# Revit family: Zumtobel VIVO II S
name_source: partatom
category: Lighting Fixtures
revit_build: Autodesk Revit 2016 (Build: 20150220_1215(x64)
units: mm (PartAtom-declared; Revit-internal decimal feet)

## family parameters
Cut with Voids When Loaded = No
Host = Face
Light Source = No
OmniClass Number = 23.80.70.11
OmniClass Title = Luminaries for Internal Lighting
Part Type = Normal
Room Calculation Point = No
Round Connector Dimension = Use Diameter
Shared = No

## types (2) — shared parameters
Apparent Load = 29 VA
Assembly Code = D5020200
Emit Shape Visible in Rendering = Yes
Lamp = LED
Manufacturer = Zumtobel Lighting
URL = http://www.zumtobel.com
zero-valued in all types: Default Elevation

## per-type parameters (varying)
| type | Body Type | Description | Model | Semi Recessed | Surface Mount |
| VIV2 S 2800-840 SWI 3VVC MSP WH WH | Zumtobel Vivo II S Body : VIV2 S 2800-840 SWI 3VVC MSP WH WH | LED spotlight | 60715474 | No | Yes |
| V2-SR S 2300-930 SWI FL WH WH | Zumtobel Vivo II S Body : V2-SR S 2300-930 SWI FL WH WH | Semi-Recessed LED spotlight | 60716703 | Yes | No |

## geometry (parser evidence)
native form markers: Sweep x4
no freeform markers — native parametric forms only
